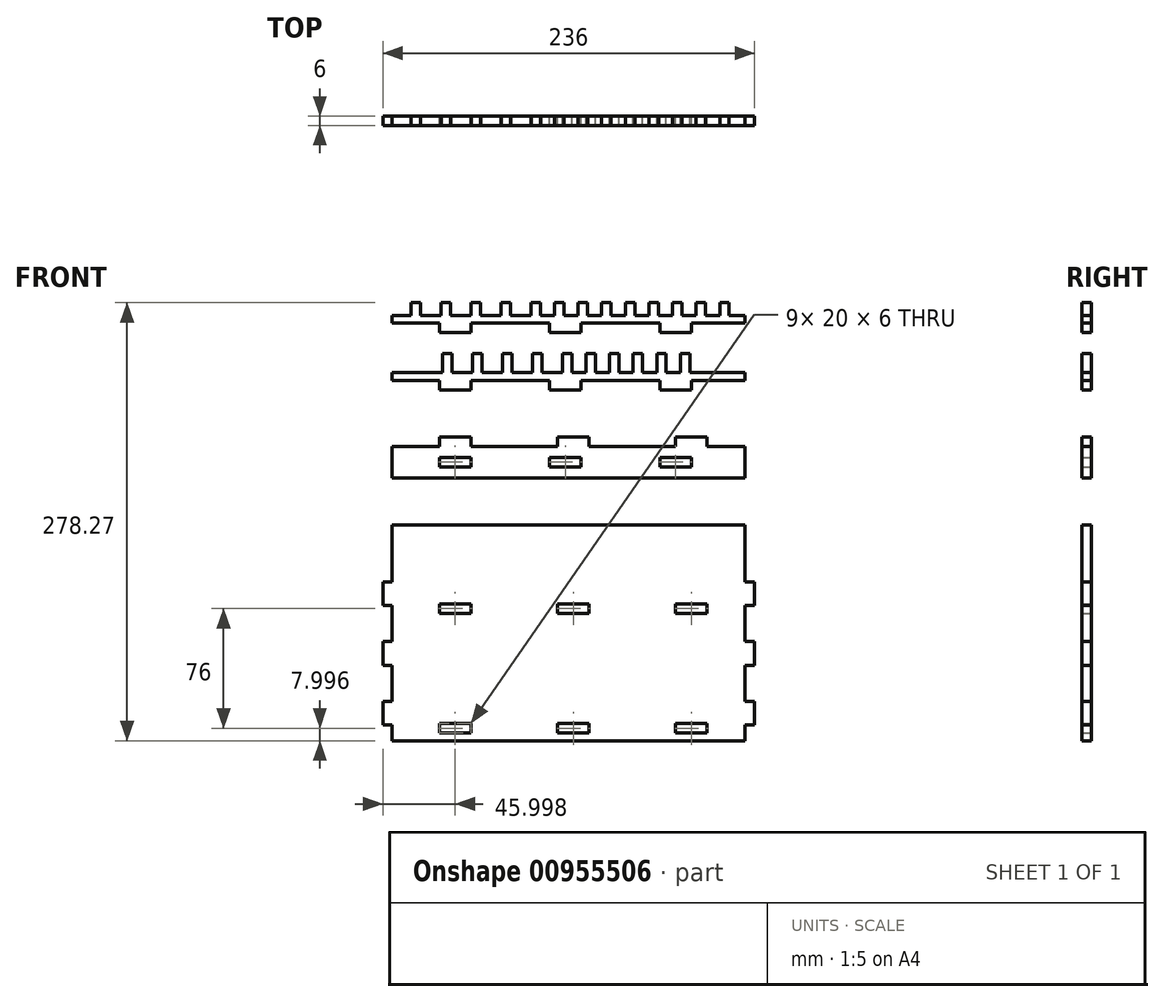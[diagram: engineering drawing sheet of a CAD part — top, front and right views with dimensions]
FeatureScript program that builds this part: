
annotation { "Feature Type Name" : "Feature", "Feature Type Description" : "" }
export const myFeature = defineFeature(function(context is Context, id is Id, definition is map)
    precondition{}
    {
        {
            var Q0;
            Q0=qCreatedBy(makeId("Front.planeOp"),FACE);
            var sketch = newSketch(context, id + "F0", { "sketchPlane" : qUnion([Q0])});
            skLineSegment(sketch, "E0", {"start": v(-79.13, 82.86) * mm, "end": v(-79.13, 90.86) * mm});
            skLineSegment(sketch, "E1", {"start": v(-79.13, 90.86) * mm, "end": v(-73.13, 90.86) * mm});
            skLineSegment(sketch, "E2", {"start": v(-73.13, 90.86) * mm, "end": v(-73.13, 82.86) * mm});
            skLineSegment(sketch, "E3", {"start": v(-73.13, 82.86) * mm, "end": v(-60.13, 82.86) * mm});
            skLineSegment(sketch, "E4.1.0.0", {"start": v(-60.13, 82.86) * mm, "end": v(-60.13, 90.86) * mm});
            skLineSegment(sketch, "E4.1.0.1", {"start": v(-60.13, 90.86) * mm, "end": v(-54.13, 90.86) * mm});
            skLineSegment(sketch, "E4.1.0.2", {"start": v(-54.13, 90.86) * mm, "end": v(-54.13, 82.86) * mm});
            skLineSegment(sketch, "E4.1.0.3", {"start": v(-54.13, 82.86) * mm, "end": v(-41.13, 82.86) * mm});
            skLineSegment(sketch, "E4.2.0.0", {"start": v(-41.13, 82.86) * mm, "end": v(-41.13, 90.86) * mm});
            skLineSegment(sketch, "E4.2.0.1", {"start": v(-41.13, 90.86) * mm, "end": v(-35.13, 90.86) * mm});
            skLineSegment(sketch, "E4.2.0.2", {"start": v(-35.13, 90.86) * mm, "end": v(-35.13, 82.86) * mm});
            skLineSegment(sketch, "E4.2.0.3", {"start": v(-35.13, 82.86) * mm, "end": v(-22.13, 82.86) * mm});
            skLineSegment(sketch, "E4.3.0.0", {"start": v(-22.13, 82.86) * mm, "end": v(-22.13, 90.86) * mm});
            skLineSegment(sketch, "E4.3.0.1", {"start": v(-22.13, 90.86) * mm, "end": v(-16.13, 90.86) * mm});
            skLineSegment(sketch, "E4.3.0.2", {"start": v(-16.13, 90.86) * mm, "end": v(-16.13, 82.86) * mm});
            skLineSegment(sketch, "E4.direction1", {"start": v(-79.13, 82.86) * mm, "end": v(-60.13, 82.86) * mm, "construction": true});
            skLineSegment(sketch, "E5", {"start": v(16.87, 46.49) * mm, "end": v(16.87, 58.49) * mm});
            skLineSegment(sketch, "E6", {"start": v(16.87, 58.49) * mm, "end": v(22.87, 58.49) * mm});
            skLineSegment(sketch, "E7", {"start": v(22.87, 58.49) * mm, "end": v(22.87, 46.49) * mm});
            skLineSegment(sketch, "E8", {"start": v(22.87, 46.49) * mm, "end": v(31.87, 46.49) * mm});
            skLineSegment(sketch, "E9.1.0.0", {"start": v(31.87, 46.49) * mm, "end": v(31.87, 58.49) * mm});
            skLineSegment(sketch, "E9.1.0.1", {"start": v(31.87, 58.49) * mm, "end": v(37.87, 58.49) * mm});
            skLineSegment(sketch, "E9.1.0.2", {"start": v(37.87, 58.49) * mm, "end": v(37.87, 46.49) * mm});
            skLineSegment(sketch, "E9.1.0.3", {"start": v(37.87, 46.49) * mm, "end": v(46.87, 46.49) * mm});
            skLineSegment(sketch, "E9.2.0.0", {"start": v(46.87, 46.49) * mm, "end": v(46.87, 58.49) * mm});
            skLineSegment(sketch, "E9.2.0.1", {"start": v(46.87, 58.49) * mm, "end": v(52.87, 58.49) * mm});
            skLineSegment(sketch, "E9.2.0.2", {"start": v(52.87, 58.49) * mm, "end": v(52.87, 46.49) * mm});
            skLineSegment(sketch, "E9.2.0.3", {"start": v(52.87, 46.49) * mm, "end": v(61.87, 46.49) * mm});
            skLineSegment(sketch, "E9.3.0.0", {"start": v(61.87, 46.49) * mm, "end": v(61.87, 58.49) * mm});
            skLineSegment(sketch, "E9.3.0.1", {"start": v(61.87, 58.49) * mm, "end": v(67.87, 58.49) * mm});
            skLineSegment(sketch, "E9.3.0.2", {"start": v(67.87, 58.49) * mm, "end": v(67.87, 46.49) * mm});
            skLineSegment(sketch, "E9.3.0.3", {"start": v(67.87, 46.49) * mm, "end": v(76.87, 46.49) * mm});
            skLineSegment(sketch, "E9.direction1", {"start": v(16.87, 46.49) * mm, "end": v(31.87, 46.49) * mm, "construction": true});
            skLineSegment(sketch, "E10", {"start": v(-3.13, 82.86) * mm, "end": v(-3.13, 90.86) * mm});
            skLineSegment(sketch, "E11", {"start": v(-3.13, 90.86) * mm, "end": v(2.87, 90.86) * mm});
            skLineSegment(sketch, "E12", {"start": v(2.87, 90.86) * mm, "end": v(2.87, 82.86) * mm});
            skLineSegment(sketch, "E13", {"start": v(2.87, 82.86) * mm, "end": v(11.87, 82.86) * mm});
            skLineSegment(sketch, "E14.1.0.0", {"start": v(11.87, 82.86) * mm, "end": v(11.87, 90.86) * mm});
            skLineSegment(sketch, "E14.1.0.1", {"start": v(11.87, 90.86) * mm, "end": v(17.87, 90.86) * mm});
            skLineSegment(sketch, "E14.1.0.2", {"start": v(17.87, 90.86) * mm, "end": v(17.87, 82.86) * mm});
            skLineSegment(sketch, "E14.1.0.3", {"start": v(17.87, 82.86) * mm, "end": v(26.87, 82.86) * mm});
            skLineSegment(sketch, "E14.2.0.0", {"start": v(26.87, 82.86) * mm, "end": v(26.87, 90.86) * mm});
            skLineSegment(sketch, "E14.2.0.1", {"start": v(26.87, 90.86) * mm, "end": v(32.87, 90.86) * mm});
            skLineSegment(sketch, "E14.2.0.2", {"start": v(32.87, 90.86) * mm, "end": v(32.87, 82.86) * mm});
            skLineSegment(sketch, "E14.2.0.3", {"start": v(32.87, 82.86) * mm, "end": v(41.87, 82.86) * mm});
            skLineSegment(sketch, "E14.3.0.0", {"start": v(41.87, 82.86) * mm, "end": v(41.87, 90.86) * mm});
            skLineSegment(sketch, "E14.3.0.1", {"start": v(41.87, 90.86) * mm, "end": v(47.87, 90.86) * mm});
            skLineSegment(sketch, "E14.3.0.2", {"start": v(47.87, 90.86) * mm, "end": v(47.87, 82.86) * mm});
            skLineSegment(sketch, "E14.3.0.3", {"start": v(47.87, 82.86) * mm, "end": v(56.87, 82.86) * mm});
            skLineSegment(sketch, "E14.direction1", {"start": v(-3.13, 82.86) * mm, "end": v(11.87, 82.86) * mm, "construction": true});
            skLineSegment(sketch, "E15", {"start": v(-59.13, 46.49) * mm, "end": v(-59.13, 58.49) * mm});
            skLineSegment(sketch, "E16", {"start": v(-59.13, 58.49) * mm, "end": v(-53.13, 58.49) * mm});
            skLineSegment(sketch, "E17", {"start": v(-53.13, 58.49) * mm, "end": v(-53.13, 46.49) * mm});
            skLineSegment(sketch, "E18", {"start": v(-53.13, 46.49) * mm, "end": v(-40.13, 46.49) * mm});
            skLineSegment(sketch, "E19.1.0.0", {"start": v(-40.13, 46.49) * mm, "end": v(-40.13, 58.49) * mm});
            skLineSegment(sketch, "E19.1.0.1", {"start": v(-40.13, 58.49) * mm, "end": v(-34.13, 58.49) * mm});
            skLineSegment(sketch, "E19.1.0.2", {"start": v(-34.13, 58.49) * mm, "end": v(-34.13, 46.49) * mm});
            skLineSegment(sketch, "E19.1.0.3", {"start": v(-34.13, 46.49) * mm, "end": v(-21.13, 46.49) * mm});
            skLineSegment(sketch, "E19.2.0.0", {"start": v(-21.13, 46.49) * mm, "end": v(-21.13, 58.49) * mm});
            skLineSegment(sketch, "E19.2.0.1", {"start": v(-21.13, 58.49) * mm, "end": v(-15.13, 58.49) * mm});
            skLineSegment(sketch, "E19.2.0.2", {"start": v(-15.13, 58.49) * mm, "end": v(-15.13, 46.49) * mm});
            skLineSegment(sketch, "E19.2.0.3", {"start": v(-15.13, 46.49) * mm, "end": v(-2.13, 46.49) * mm});
            skLineSegment(sketch, "E19.3.0.0", {"start": v(-2.13, 46.49) * mm, "end": v(-2.13, 58.49) * mm});
            skLineSegment(sketch, "E19.3.0.1", {"start": v(-2.13, 58.49) * mm, "end": v(3.87, 58.49) * mm});
            skLineSegment(sketch, "E19.3.0.2", {"start": v(3.87, 58.49) * mm, "end": v(3.87, 46.49) * mm});
            skLineSegment(sketch, "E19.direction1", {"start": v(-59.13, 46.49) * mm, "end": v(-40.13, 46.49) * mm, "construction": true});
            skLineSegment(sketch, "E20.0.4.0", {"start": v(76.87, 46.49) * mm, "end": v(76.87, 58.49) * mm});
            skLineSegment(sketch, "E20.3.4.0", {"start": v(76.87, 58.49) * mm, "end": v(82.87, 58.49) * mm});
            skLineSegment(sketch, "E20.6.4.0", {"start": v(82.87, 58.49) * mm, "end": v(82.87, 46.49) * mm});
            skLineSegment(sketch, "E20.9.4.0", {"start": v(82.87, 46.49) * mm, "end": v(91.87, 46.49) * mm});
            skLineSegment(sketch, "E20.0.5.0", {"start": v(91.87, 46.49) * mm, "end": v(91.87, 58.49) * mm});
            skLineSegment(sketch, "E20.3.5.0", {"start": v(91.87, 58.49) * mm, "end": v(97.87, 58.49) * mm});
            skLineSegment(sketch, "E20.6.5.0", {"start": v(97.87, 58.49) * mm, "end": v(97.87, 46.49) * mm});
            skLineSegment(sketch, "E21.0.4.0", {"start": v(56.87, 82.86) * mm, "end": v(56.87, 90.86) * mm});
            skLineSegment(sketch, "E21.3.4.0", {"start": v(56.87, 90.86) * mm, "end": v(62.87, 90.86) * mm});
            skLineSegment(sketch, "E21.6.4.0", {"start": v(62.87, 90.86) * mm, "end": v(62.87, 82.86) * mm});
            skLineSegment(sketch, "E21.9.4.0", {"start": v(62.87, 82.86) * mm, "end": v(71.87, 82.86) * mm});
            skLineSegment(sketch, "E21.0.5.0", {"start": v(71.87, 82.86) * mm, "end": v(71.87, 90.86) * mm});
            skLineSegment(sketch, "E21.3.5.0", {"start": v(71.87, 90.86) * mm, "end": v(77.87, 90.86) * mm});
            skLineSegment(sketch, "E21.6.5.0", {"start": v(77.87, 90.86) * mm, "end": v(77.87, 82.86) * mm});
            skLineSegment(sketch, "E21.9.5.0", {"start": v(77.87, 82.86) * mm, "end": v(86.87, 82.86) * mm});
            skLineSegment(sketch, "E21.0.6.0", {"start": v(86.87, 82.86) * mm, "end": v(86.87, 90.86) * mm});
            skLineSegment(sketch, "E21.3.6.0", {"start": v(86.87, 90.86) * mm, "end": v(92.87, 90.86) * mm});
            skLineSegment(sketch, "E21.6.6.0", {"start": v(92.87, 90.86) * mm, "end": v(92.87, 82.86) * mm});
            skLineSegment(sketch, "E21.9.6.0", {"start": v(92.87, 82.86) * mm, "end": v(101.87, 82.86) * mm});
            skLineSegment(sketch, "E21.0.7.0", {"start": v(101.87, 82.86) * mm, "end": v(101.87, 90.86) * mm});
            skLineSegment(sketch, "E21.3.7.0", {"start": v(101.87, 90.86) * mm, "end": v(107.87, 90.86) * mm});
            skLineSegment(sketch, "E21.6.7.0", {"start": v(107.87, 90.86) * mm, "end": v(107.87, 82.86) * mm});
            skLineSegment(sketch, "E21.9.7.0", {"start": v(107.87, 82.86) * mm, "end": v(116.87, 82.86) * mm});
            skLineSegment(sketch, "E21.0.8.0", {"start": v(116.87, 82.86) * mm, "end": v(116.87, 90.86) * mm});
            skLineSegment(sketch, "E21.3.8.0", {"start": v(116.87, 90.86) * mm, "end": v(122.87, 90.86) * mm});
            skLineSegment(sketch, "E21.6.8.0", {"start": v(122.87, 90.86) * mm, "end": v(122.87, 82.86) * mm});
            skLineSegment(sketch, "E22", {"start": v(-16.13, 82.86) * mm, "end": v(-3.13, 82.86) * mm});
            skLineSegment(sketch, "E23", {"start": v(3.87, 46.49) * mm, "end": v(16.87, 46.49) * mm});
            skLineSegment(sketch, "E24", {"start": v(-79.13, 82.86) * mm, "end": v(-91.13, 82.86) * mm});
            skLineSegment(sketch, "E25", {"start": v(-91.13, 82.86) * mm, "end": v(-91.13, 77.86) * mm});
            skLineSegment(sketch, "E26", {"start": v(-91.13, 77.86) * mm, "end": v(-61.13, 77.86) * mm});
            skLineSegment(sketch, "E27", {"start": v(132.87, 77.86) * mm, "end": v(132.87, 82.86) * mm});
            skLineSegment(sketch, "E28", {"start": v(132.87, 82.86) * mm, "end": v(122.87, 82.86) * mm});
            skLineSegment(sketch, "E29", {"start": v(-59.13, 46.49) * mm, "end": v(-91.13, 46.49) * mm});
            skLineSegment(sketch, "E30", {"start": v(-91.13, 46.49) * mm, "end": v(-91.13, 41.49) * mm});
            skLineSegment(sketch, "E31", {"start": v(-91.13, 41.49) * mm, "end": v(-61.13, 41.49) * mm});
            skLineSegment(sketch, "E32", {"start": v(132.87, 41.49) * mm, "end": v(132.87, 46.49) * mm});
            skLineSegment(sketch, "E33", {"start": v(132.87, 46.49) * mm, "end": v(97.87, 46.49) * mm});
            skLineSegment(sketch, "E34.top", {"start": v(-61.13, 71.86) * mm, "end": v(-41.13, 71.86) * mm});
            skLineSegment(sketch, "E34.left", {"start": v(-61.13, 77.86) * mm, "end": v(-61.13, 71.86) * mm});
            skLineSegment(sketch, "E34.right", {"start": v(-41.13, 77.86) * mm, "end": v(-41.13, 71.86) * mm});
            skLineSegment(sketch, "E35.top", {"start": v(-61.13, 35.49) * mm, "end": v(-41.13, 35.49) * mm});
            skLineSegment(sketch, "E35.left", {"start": v(-61.13, 41.49) * mm, "end": v(-61.13, 35.49) * mm});
            skLineSegment(sketch, "E35.right", {"start": v(-41.13, 41.49) * mm, "end": v(-41.13, 35.49) * mm});
            skLineSegment(sketch, "E36.1.0.0", {"start": v(8.87, 77.86) * mm, "end": v(8.87, 71.86) * mm});
            skLineSegment(sketch, "E36.1.0.1", {"start": v(8.87, 71.86) * mm, "end": v(28.87, 71.86) * mm});
            skLineSegment(sketch, "E36.1.0.2", {"start": v(28.87, 77.86) * mm, "end": v(28.87, 71.86) * mm});
            skLineSegment(sketch, "E36.2.0.0", {"start": v(78.87, 77.86) * mm, "end": v(78.87, 71.86) * mm});
            skLineSegment(sketch, "E36.2.0.1", {"start": v(78.87, 71.86) * mm, "end": v(98.87, 71.86) * mm});
            skLineSegment(sketch, "E36.2.0.2", {"start": v(98.87, 77.86) * mm, "end": v(98.87, 71.86) * mm});
            skLineSegment(sketch, "E36.direction1", {"start": v(-61.13, 71.86) * mm, "end": v(8.87, 71.86) * mm, "construction": true});
            skLineSegment(sketch, "E37.1.0.0", {"start": v(8.87, 41.49) * mm, "end": v(8.87, 35.49) * mm});
            skLineSegment(sketch, "E37.1.0.1", {"start": v(8.87, 35.49) * mm, "end": v(28.87, 35.49) * mm});
            skLineSegment(sketch, "E37.1.0.2", {"start": v(28.87, 41.49) * mm, "end": v(28.87, 35.49) * mm});
            skLineSegment(sketch, "E37.2.0.0", {"start": v(78.87, 41.49) * mm, "end": v(78.87, 35.49) * mm});
            skLineSegment(sketch, "E37.2.0.1", {"start": v(78.87, 35.49) * mm, "end": v(98.87, 35.49) * mm});
            skLineSegment(sketch, "E37.2.0.2", {"start": v(98.87, 41.49) * mm, "end": v(98.87, 35.49) * mm});
            skLineSegment(sketch, "E37.direction1", {"start": v(-61.13, 35.49) * mm, "end": v(8.87, 35.49) * mm, "construction": true});
            skLineSegment(sketch, "E38.trimOffspring", {"start": v(-41.13, 77.86) * mm, "end": v(8.87, 77.86) * mm});
            skLineSegment(sketch, "E39.trimOffspring", {"start": v(28.87, 77.86) * mm, "end": v(78.87, 77.86) * mm});
            skLineSegment(sketch, "E40.trimOffspring", {"start": v(98.87, 77.86) * mm, "end": v(132.87, 77.86) * mm});
            skLineSegment(sketch, "E41.trimOffspring", {"start": v(98.87, 41.49) * mm, "end": v(132.87, 41.49) * mm});
            skLineSegment(sketch, "E42.trimOffspring", {"start": v(28.87, 41.49) * mm, "end": v(78.87, 41.49) * mm});
            skLineSegment(sketch, "E43.trimOffspring", {"start": v(-41.13, 41.49) * mm, "end": v(8.87, 41.49) * mm});
            skLineSegment(sketch, "E44.bottom", {"start": v(-91.13, -0.41) * mm, "end": v(-61.13, -0.41) * mm});
            skLineSegment(sketch, "E44.top", {"start": v(-91.13, -20.41) * mm, "end": v(132.87, -20.41) * mm});
            skLineSegment(sketch, "E44.left", {"start": v(-91.13, -0.41) * mm, "end": v(-91.13, -20.41) * mm});
            skLineSegment(sketch, "E44.right", {"start": v(132.87, -0.41) * mm, "end": v(132.87, -20.41) * mm});
            skLineSegment(sketch, "E45", {"start": v(-91.13, -10.41) * mm, "end": v(132.87, -10.41) * mm, "construction": true});
            skLineSegment(sketch, "E46.bottom", {"start": v(-61.13, -7.41) * mm, "end": v(-41.13, -7.41) * mm});
            skLineSegment(sketch, "E46.top", {"start": v(-61.13, -13.41) * mm, "end": v(-41.13, -13.41) * mm});
            skLineSegment(sketch, "E46.left", {"start": v(-61.13, -7.41) * mm, "end": v(-61.13, -13.41) * mm});
            skLineSegment(sketch, "E46.right", {"start": v(-41.13, -7.41) * mm, "end": v(-41.13, -13.41) * mm});
            skPoint(sketch, "E46.middle", {"position": v(-51.13, -10.41) * mm});
            skLineSegment(sketch, "E47.1.0.0", {"start": v(8.87, -7.41) * mm, "end": v(28.87, -7.41) * mm});
            skLineSegment(sketch, "E47.1.0.1", {"start": v(8.87, -7.41) * mm, "end": v(8.87, -13.41) * mm});
            skLineSegment(sketch, "E47.1.0.2", {"start": v(8.87, -13.41) * mm, "end": v(28.87, -13.41) * mm});
            skLineSegment(sketch, "E47.1.0.3", {"start": v(28.87, -7.41) * mm, "end": v(28.87, -13.41) * mm});
            skLineSegment(sketch, "E47.2.0.0", {"start": v(78.87, -7.41) * mm, "end": v(98.87, -7.41) * mm});
            skLineSegment(sketch, "E47.2.0.1", {"start": v(78.87, -7.41) * mm, "end": v(78.87, -13.41) * mm});
            skLineSegment(sketch, "E47.2.0.2", {"start": v(78.87, -13.41) * mm, "end": v(98.87, -13.41) * mm});
            skLineSegment(sketch, "E47.2.0.3", {"start": v(98.87, -7.41) * mm, "end": v(98.87, -13.41) * mm});
            skLineSegment(sketch, "E47.direction1", {"start": v(-61.13, -7.41) * mm, "end": v(8.87, -7.41) * mm, "construction": true});
            skLineSegment(sketch, "E48.top", {"start": v(-61.13, 5.59) * mm, "end": v(-41.13, 5.59) * mm});
            skLineSegment(sketch, "E48.left", {"start": v(-61.13, -0.41) * mm, "end": v(-61.13, 5.59) * mm});
            skLineSegment(sketch, "E48.right", {"start": v(-41.13, -0.41) * mm, "end": v(-41.13, 5.59) * mm});
            skLineSegment(sketch, "E49.1.0.0", {"start": v(13.87, -0.41) * mm, "end": v(13.87, 5.59) * mm});
            skLineSegment(sketch, "E49.1.0.1", {"start": v(13.87, 5.59) * mm, "end": v(33.87, 5.59) * mm});
            skLineSegment(sketch, "E49.1.0.2", {"start": v(33.87, -0.41) * mm, "end": v(33.87, 5.59) * mm});
            skLineSegment(sketch, "E49.2.0.0", {"start": v(88.87, -0.41) * mm, "end": v(88.87, 5.59) * mm});
            skLineSegment(sketch, "E49.2.0.1", {"start": v(88.87, 5.59) * mm, "end": v(108.87, 5.59) * mm});
            skLineSegment(sketch, "E49.2.0.2", {"start": v(108.87, -0.41) * mm, "end": v(108.87, 5.59) * mm});
            skLineSegment(sketch, "E49.direction1", {"start": v(-41.13, -0.41) * mm, "end": v(13.87, -0.41) * mm, "construction": true});
            skLineSegment(sketch, "E50.trimOffspring", {"start": v(-41.13, -0.41) * mm, "end": v(13.87, -0.41) * mm});
            skLineSegment(sketch, "E51.trimOffspring", {"start": v(33.87, -0.41) * mm, "end": v(88.87, -0.41) * mm});
            skLineSegment(sketch, "E52.trimOffspring", {"start": v(108.87, -0.41) * mm, "end": v(132.87, -0.41) * mm});
            skLineSegment(sketch, "E53.bottom", {"start": v(-91.13, -50.41) * mm, "end": v(132.87, -50.41) * mm});
            skLineSegment(sketch, "E53.top", {"start": v(-91.13, -187.41) * mm, "end": v(132.87, -187.41) * mm});
            skLineSegment(sketch, "E53.left", {"start": v(-91.13, -50.41) * mm, "end": v(-91.13, -86.41) * mm});
            skLineSegment(sketch, "E53.right", {"start": v(132.87, -50.41) * mm, "end": v(132.87, -86.41) * mm});
            skLineSegment(sketch, "E54", {"start": v(-91.13, -103.41) * mm, "end": v(132.87, -103.41) * mm, "construction": true});
            skLineSegment(sketch, "E55", {"start": v(-91.13, -179.41) * mm, "end": v(132.87, -179.41) * mm, "construction": true});
            skLineSegment(sketch, "E56.bottom", {"start": v(-41.13, -106.41) * mm, "end": v(-61.13, -106.41) * mm});
            skLineSegment(sketch, "E56.top", {"start": v(-41.13, -100.41) * mm, "end": v(-61.13, -100.41) * mm});
            skLineSegment(sketch, "E56.left", {"start": v(-41.13, -106.41) * mm, "end": v(-41.13, -100.41) * mm});
            skLineSegment(sketch, "E56.right", {"start": v(-61.13, -106.41) * mm, "end": v(-61.13, -100.41) * mm});
            skPoint(sketch, "E56.middle", {"position": v(-51.13, -103.41) * mm});
            skLineSegment(sketch, "E57.bottom", {"start": v(-41.13, -176.41) * mm, "end": v(-61.13, -176.41) * mm});
            skLineSegment(sketch, "E57.top", {"start": v(-41.13, -182.41) * mm, "end": v(-61.13, -182.41) * mm});
            skLineSegment(sketch, "E57.left", {"start": v(-41.13, -176.41) * mm, "end": v(-41.13, -182.41) * mm});
            skLineSegment(sketch, "E57.right", {"start": v(-61.13, -176.41) * mm, "end": v(-61.13, -182.41) * mm});
            skPoint(sketch, "E57.middle", {"position": v(-51.13, -179.41) * mm});
            skLineSegment(sketch, "E58.1.0.0", {"start": v(33.87, -100.41) * mm, "end": v(13.87, -100.41) * mm});
            skLineSegment(sketch, "E58.1.0.1", {"start": v(13.87, -106.41) * mm, "end": v(13.87, -100.41) * mm});
            skLineSegment(sketch, "E58.1.0.2", {"start": v(33.87, -106.41) * mm, "end": v(13.87, -106.41) * mm});
            skLineSegment(sketch, "E58.1.0.3", {"start": v(33.87, -106.41) * mm, "end": v(33.87, -100.41) * mm});
            skLineSegment(sketch, "E58.2.0.0", {"start": v(108.87, -100.41) * mm, "end": v(88.87, -100.41) * mm});
            skLineSegment(sketch, "E58.2.0.1", {"start": v(88.87, -106.41) * mm, "end": v(88.87, -100.41) * mm});
            skLineSegment(sketch, "E58.2.0.2", {"start": v(108.87, -106.41) * mm, "end": v(88.87, -106.41) * mm});
            skLineSegment(sketch, "E58.2.0.3", {"start": v(108.87, -106.41) * mm, "end": v(108.87, -100.41) * mm});
            skLineSegment(sketch, "E58.direction1", {"start": v(-61.13, -100.41) * mm, "end": v(13.87, -100.41) * mm, "construction": true});
            skLineSegment(sketch, "E59.1.0.0", {"start": v(13.87, -176.41) * mm, "end": v(13.87, -182.41) * mm});
            skLineSegment(sketch, "E59.1.0.1", {"start": v(33.87, -176.41) * mm, "end": v(13.87, -176.41) * mm});
            skLineSegment(sketch, "E59.1.0.2", {"start": v(33.87, -176.41) * mm, "end": v(33.87, -182.41) * mm});
            skLineSegment(sketch, "E59.1.0.3", {"start": v(33.87, -182.41) * mm, "end": v(13.87, -182.41) * mm});
            skLineSegment(sketch, "E59.2.0.0", {"start": v(88.87, -176.41) * mm, "end": v(88.87, -182.41) * mm});
            skLineSegment(sketch, "E59.2.0.1", {"start": v(108.87, -176.41) * mm, "end": v(88.87, -176.41) * mm});
            skLineSegment(sketch, "E59.2.0.2", {"start": v(108.87, -176.41) * mm, "end": v(108.87, -182.41) * mm});
            skLineSegment(sketch, "E59.2.0.3", {"start": v(108.87, -182.41) * mm, "end": v(88.87, -182.41) * mm});
            skLineSegment(sketch, "E59.direction1", {"start": v(-61.13, -182.41) * mm, "end": v(13.87, -182.41) * mm, "construction": true});
            skLineSegment(sketch, "E60.bottom", {"start": v(-91.13, -86.41) * mm, "end": v(-97.13, -86.41) * mm});
            skLineSegment(sketch, "E60.top", {"start": v(-91.13, -101.41) * mm, "end": v(-97.13, -101.41) * mm});
            skLineSegment(sketch, "E60.right", {"start": v(-97.13, -86.41) * mm, "end": v(-97.13, -101.41) * mm});
            skLineSegment(sketch, "E61.0.1.0", {"start": v(-91.13, -124.41) * mm, "end": v(-97.13, -124.41) * mm});
            skLineSegment(sketch, "E61.0.1.2", {"start": v(-91.13, -139.41) * mm, "end": v(-97.13, -139.41) * mm});
            skLineSegment(sketch, "E61.0.1.3", {"start": v(-97.13, -124.41) * mm, "end": v(-97.13, -139.41) * mm});
            skLineSegment(sketch, "E61.0.2.0", {"start": v(-91.13, -162.41) * mm, "end": v(-97.13, -162.41) * mm});
            skLineSegment(sketch, "E61.0.2.2", {"start": v(-91.13, -177.41) * mm, "end": v(-97.13, -177.41) * mm});
            skLineSegment(sketch, "E61.0.2.3", {"start": v(-97.13, -162.41) * mm, "end": v(-97.13, -177.41) * mm});
            skLineSegment(sketch, "E61.1.0.0", {"start": v(138.87, -86.41) * mm, "end": v(132.87, -86.41) * mm});
            skLineSegment(sketch, "E61.1.0.1", {"start": v(138.87, -86.41) * mm, "end": v(138.87, -101.41) * mm});
            skLineSegment(sketch, "E61.1.0.2", {"start": v(138.87, -101.41) * mm, "end": v(132.87, -101.41) * mm});
            skLineSegment(sketch, "E61.1.1.0", {"start": v(138.87, -124.41) * mm, "end": v(132.87, -124.41) * mm});
            skLineSegment(sketch, "E61.1.1.1", {"start": v(138.87, -124.41) * mm, "end": v(138.87, -139.41) * mm});
            skLineSegment(sketch, "E61.1.1.2", {"start": v(138.87, -139.41) * mm, "end": v(132.87, -139.41) * mm});
            skLineSegment(sketch, "E61.1.2.0", {"start": v(138.87, -162.41) * mm, "end": v(132.87, -162.41) * mm});
            skLineSegment(sketch, "E61.1.2.1", {"start": v(138.87, -162.41) * mm, "end": v(138.87, -177.41) * mm});
            skLineSegment(sketch, "E61.1.2.2", {"start": v(138.87, -177.41) * mm, "end": v(132.87, -177.41) * mm});
            skLineSegment(sketch, "E61.direction1", {"start": v(-97.13, -86.41) * mm, "end": v(132.87, -86.41) * mm, "construction": true});
            skLineSegment(sketch, "E61.direction2", {"start": v(-97.13, -86.41) * mm, "end": v(-97.13, -124.41) * mm, "construction": true});
            skLineSegment(sketch, "E62.trimOffspring", {"start": v(-91.13, -139.41) * mm, "end": v(-91.13, -162.41) * mm});
            skLineSegment(sketch, "E63.trimOffspring", {"start": v(-91.13, -177.41) * mm, "end": v(-91.13, -187.41) * mm});
            skLineSegment(sketch, "E64.trimOffspring", {"start": v(132.87, -101.41) * mm, "end": v(132.87, -124.41) * mm});
            skLineSegment(sketch, "E65.trimOffspring", {"start": v(132.87, -177.41) * mm, "end": v(132.87, -187.41) * mm});
            skLineSegment(sketch, "E66.trimOffspring", {"start": v(132.87, -139.41) * mm, "end": v(132.87, -162.41) * mm});
            skLineSegment(sketch, "E67.trimOffspring", {"start": v(-91.13, -101.41) * mm, "end": v(-91.13, -124.41) * mm});
            skSolve(sketch);
        }
        {
            var Q0;
            Q0=makeQuery(id+"F0.imprint","IMPRINT",FACE,{"disambiguationData":[TD([[makeQuery(id+"F0.imprint","IMPRINT",EDGE,{"derivedFrom":sQuery(id+"F0.wireOp",EDGE,"E53.bottom")}),-1.0]])]});
            extrude(context, id + "F1", {"entities" : qUnion([Q0]), "depth" : 6 * mm, "offsetDistance" : 25 * mm});
        }
        {
            var Q0;
            Q0=makeQuery(id+"F0.imprint","IMPRINT",FACE,{"disambiguationData":[TD([[makeQuery(id+"F0.imprint","IMPRINT",EDGE,{"derivedFrom":sQuery(id+"F0.wireOp",EDGE,"E44.bottom")}),-1.0]])]});
            extrude(context, id + "F2", {"entities" : qUnion([Q0]), "depth" : 6 * mm, "offsetDistance" : 25 * mm});
        }
        {
            var Q0;
            Q0=makeQuery(id+"F0.imprint","IMPRINT",FACE,{"disambiguationData":[TD([[makeQuery(id+"F0.imprint","IMPRINT",EDGE,{"derivedFrom":sQuery(id+"F0.wireOp",EDGE,"E5")}),-1.0]])]});
            extrude(context, id + "F3", {"entities" : qUnion([Q0]), "depth" : 6 * mm, "offsetDistance" : 25 * mm});
        }
        {
            var Q0;
            Q0=makeQuery(id+"F0.imprint","IMPRINT",FACE,{"disambiguationData":[TD([[makeQuery(id+"F0.imprint","IMPRINT",EDGE,{"derivedFrom":sQuery(id+"F0.wireOp",EDGE,"E0")}),-1.0]])]});
            extrude(context, id + "F4", {"entities" : qUnion([Q0]), "depth" : 6 * mm, "offsetDistance" : 25 * mm});
        }
    });
